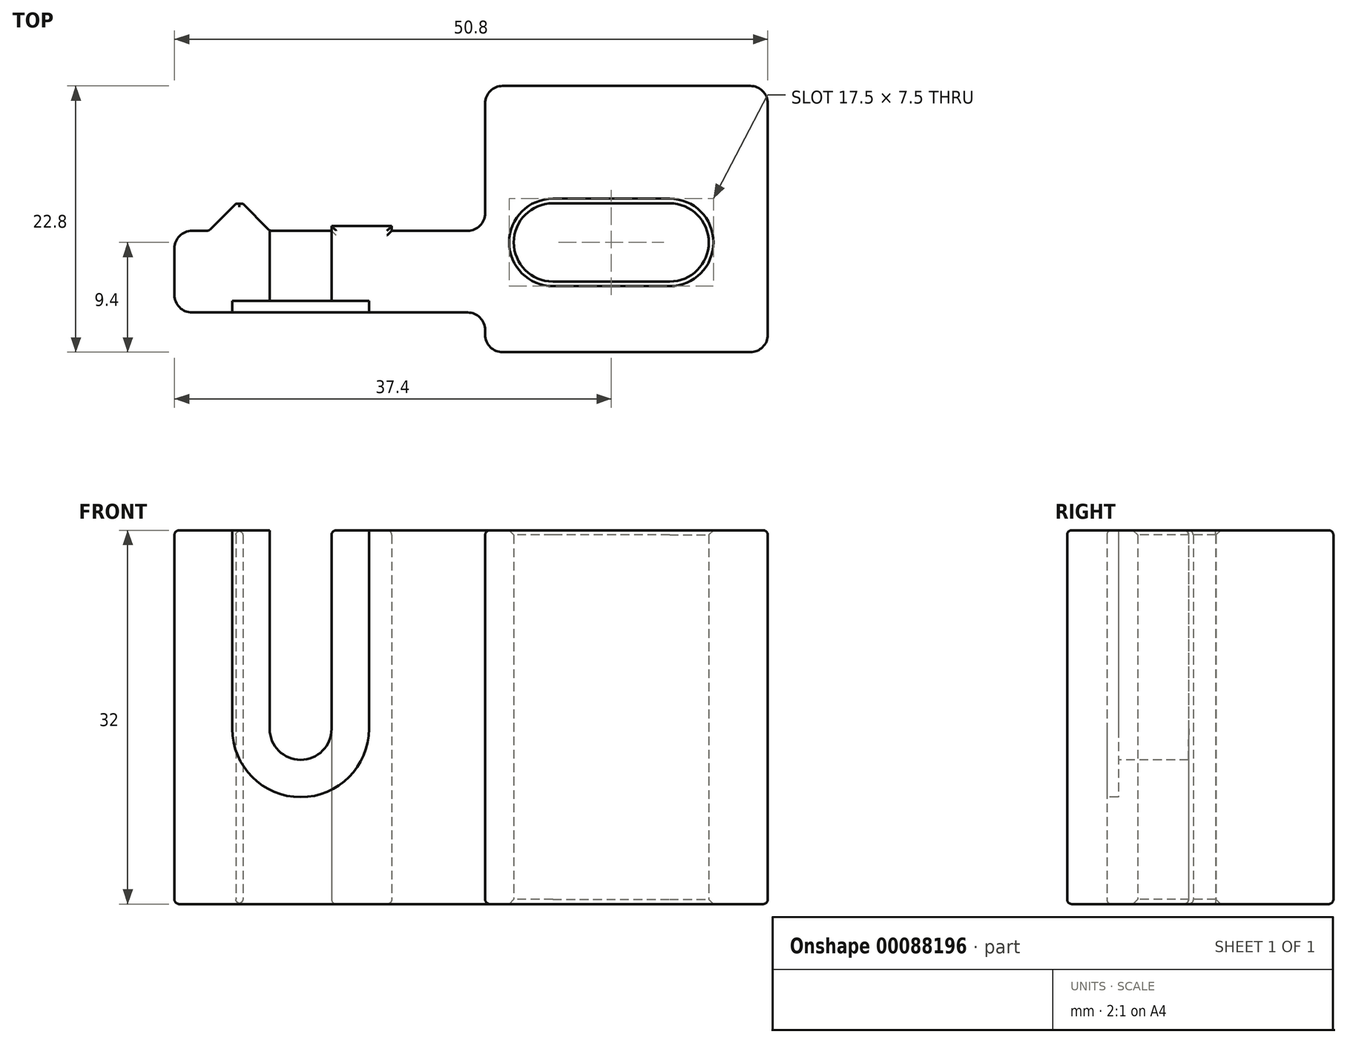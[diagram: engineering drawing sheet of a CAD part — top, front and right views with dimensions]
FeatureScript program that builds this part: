
annotation { "Feature Type Name" : "Feature", "Feature Type Description" : "" }
export const myFeature = defineFeature(function(context is Context, id is Id, definition is map)
    precondition{}
    {
        {
            var Q0;
            Q0=qCreatedBy(makeId("Top.planeOp"),FACE);
            var sketch = newSketch(context, id + "F0", { "sketchPlane" : qUnion([Q0])});
            skLineSegment(sketch, "E0", {"start": v(-10.8, 0) * mm, "end": v(-7.85, 0) * mm});
            skLineSegment(sketch, "E1", {"start": v(-2.65, 0) * mm, "end": v(2.65, 0) * mm});
            skLineSegment(sketch, "E2", {"start": v(2.65, 0) * mm, "end": v(2.65, 0.4) * mm});
            skLineSegment(sketch, "E3", {"start": v(2.65, 0.4) * mm, "end": v(7.8, 0.4) * mm});
            skLineSegment(sketch, "E4", {"start": v(7.8, 0.4) * mm, "end": v(7.8, 0) * mm});
            skLineSegment(sketch, "E5", {"start": v(7.8, 0) * mm, "end": v(15.8, 0) * mm});
            skLineSegment(sketch, "E6", {"start": v(15.8, 0) * mm, "end": v(15.8, 12.4) * mm});
            skLineSegment(sketch, "E7", {"start": v(15.8, 12.4) * mm, "end": v(40, 12.4) * mm});
            skLineSegment(sketch, "E8", {"start": v(40, 12.4) * mm, "end": v(40, -10.4) * mm});
            skLineSegment(sketch, "E9", {"start": v(40, -10.4) * mm, "end": v(15.8, -10.4) * mm});
            skLineSegment(sketch, "E10", {"start": v(15.8, -10.4) * mm, "end": v(15.8, -7) * mm});
            skLineSegment(sketch, "E11", {"start": v(15.8, -7) * mm, "end": v(-10.8, -7) * mm});
            skLineSegment(sketch, "E12", {"start": v(-10.8, -7) * mm, "end": v(-10.8, 0) * mm});
            skArc(sketch, "E13", {"start": v(21.6, 2.35) * mm, "mid": v(18.25, -1) * mm, "end": v(21.6, -4.35) * mm});
            skLineSegment(sketch, "E14", {"start": v(-7.85, 0) * mm, "end": v(-5.55, 2.3) * mm});
            skLineSegment(sketch, "E15", {"start": v(-4.95, 2.3) * mm, "end": v(-2.65, 0) * mm});
            skArc(sketch, "E16", {"start": v(31.6, -4.35) * mm, "mid": v(34.95, -1) * mm, "end": v(31.6, 2.35) * mm});
            skLineSegment(sketch, "E17", {"start": v(21.6, 2.35) * mm, "end": v(31.6, 2.35) * mm});
            skLineSegment(sketch, "E18", {"start": v(21.6, -4.35) * mm, "end": v(31.6, -4.35) * mm});
            skLineSegment(sketch, "E19", {"start": v(-5.55, 2.3) * mm, "end": v(-4.95, 2.3) * mm});
            skPoint(sketch, "E20.orphan", {"position": v(-5.25, 2.6) * mm});
            skSolve(sketch);
        }
        {
            var Q0;
            Q0=makeQuery(id+"F0.imprint","IMPRINT",FACE,{"disambiguationData":[TD([[makeQuery(id+"F0.imprint","IMPRINT",EDGE,{"derivedFrom":sQuery(id+"F0.wireOp",EDGE,"E0")}),-1.0]])]});
            extrude(context, id + "F1", {"entities" : qUnion([Q0]), "depth" : 32 * mm});
        }
        {
            var Q0;
            Q0=makeQuery(id+"F1.opExtrude","SWEPT_EDGE",EDGE,{"disambiguationData":[OSD([sQuery(id+"F0.wireOp",EDGE,"E0"),sQuery(id+"F0.wireOp",EDGE,"E14")])]});
            var Q1;
            Q1=makeQuery(id+"F1.opExtrude","SWEPT_EDGE",EDGE,{"disambiguationData":[OSD([sQuery(id+"F0.wireOp",EDGE,"E1"),sQuery(id+"F0.wireOp",EDGE,"E15")])]});
            fillet(context, id + "F2", {"entities" : qUnion([Q0, Q1]), "radius" : 0.4 * mm, "tangentPropagation" : true, "allowEdgeOverflow" : false});
        }
        {
            var Q0;
            Q0=makeQuery(id+"F1.opExtrude","SWEPT_EDGE",EDGE,{"disambiguationData":[OSD([sQuery(id+"F0.wireOp",EDGE,"E0"),sQuery(id+"F0.wireOp",EDGE,"E12")])]});
            var Q1;
            Q1=makeQuery(id+"F1.opExtrude","SWEPT_EDGE",EDGE,{"disambiguationData":[OSD([sQuery(id+"F0.wireOp",EDGE,"E11"),sQuery(id+"F0.wireOp",EDGE,"E12")])]});
            var Q2;
            Q2=makeQuery(id+"F1.opExtrude","SWEPT_EDGE",EDGE,{"disambiguationData":[OSD([sQuery(id+"F0.wireOp",EDGE,"E6"),sQuery(id+"F0.wireOp",EDGE,"E7")])]});
            var Q3;
            Q3=makeQuery(id+"F1.opExtrude","SWEPT_EDGE",EDGE,{"disambiguationData":[OSD([sQuery(id+"F0.wireOp",EDGE,"E7"),sQuery(id+"F0.wireOp",EDGE,"E8")])]});
            var Q4;
            Q4=makeQuery(id+"F1.opExtrude","SWEPT_EDGE",EDGE,{"disambiguationData":[OSD([sQuery(id+"F0.wireOp",EDGE,"E9"),sQuery(id+"F0.wireOp",EDGE,"E10")])]});
            var Q5;
            Q5=makeQuery(id+"F1.opExtrude","SWEPT_EDGE",EDGE,{"disambiguationData":[OSD([sQuery(id+"F0.wireOp",EDGE,"E8"),sQuery(id+"F0.wireOp",EDGE,"E9")])]});
            var Q6;
            Q6=makeQuery(id+"F1.opExtrude","SWEPT_EDGE",EDGE,{"disambiguationData":[OSD([sQuery(id+"F0.wireOp",EDGE,"E10"),sQuery(id+"F0.wireOp",EDGE,"E11")])]});
            var Q7;
            Q7=makeQuery(id+"F1.opExtrude","SWEPT_EDGE",EDGE,{"disambiguationData":[OSD([sQuery(id+"F0.wireOp",EDGE,"E5"),sQuery(id+"F0.wireOp",EDGE,"E6")])]});
            fillet(context, id + "F3", {"entities" : qUnion([Q0, Q1, Q2, Q3, Q4, Q5, Q6, Q7]), "radius" : 1.5 * mm, "tangentPropagation" : true, "allowEdgeOverflow" : false});
        }
        {
            var Q0;
            Q0=makeQuery(id+"F1.opExtrude","SWEPT_FACE",FACE,{"disambiguationData":[OSD([sQuery(id+"F0.wireOp",EDGE,"E11")])]});
            var sketch = newSketch(context, id + "F4", { "sketchPlane" : qUnion([Q0])});
            skLineSegment(sketch, "E21.left", {"start": v(2.65, 32) * mm, "end": v(2.65, 15) * mm});
            skLineSegment(sketch, "E21.right", {"start": v(-2.65, 32) * mm, "end": v(-2.65, 15) * mm});
            skArc(sketch, "E22", {"start": v(-2.65, 15) * mm, "mid": v(0, 12.35) * mm, "end": v(2.65, 15) * mm});
            skLineSegment(sketch, "E23", {"start": v(-5.85, 32) * mm, "end": v(-5.85, 15) * mm});
            skLineSegment(sketch, "E24", {"start": v(5.85, 32) * mm, "end": v(5.85, 15) * mm});
            skArc(sketch, "E25", {"start": v(-5.85, 15) * mm, "mid": v(0, 9.15) * mm, "end": v(5.85, 15) * mm});
            skSolve(sketch);
        }
        {
            var Q0;
            {var subQ0=sQuery(id+"F4.wireOp",EDGE,"E21.left");Q0=makeQuery(id+"F4.imprint","IMPRINT",FACE,{"disambiguationData":[TD([[makeQuery(id+"F4.imprint","IMPRINT",EDGE,{"derivedFrom":subQ0}),-1.0]])]});}
            extrude(context, id + "F5", {"entities" : qUnion([Q0]), "operationType" : NewBodyOperationType.REMOVE, "endBound" : BoundingType.THROUGH_ALL, "oppositeDirection" : true, "depth" : 25 * mm});
        }
        {
            var Q0;
            {var subQ1=sQuery(id+"F4.wireOp",EDGE,"E21.left");Q0=makeQuery(id+"F4.imprint","IMPRINT",FACE,{"disambiguationData":[TD([[makeQuery(id+"F4.imprint","IMPRINT",EDGE,{"derivedFrom":subQ1}),1.0]])]});}
            extrude(context, id + "F6", {"entities" : qUnion([Q0]), "operationType" : NewBodyOperationType.REMOVE, "oppositeDirection" : true, "depth" : 1 * mm});
        }
        {
            var Q0;
            {var subQ0=sQuery(id+"F0.wireOp",EDGE,"E12");var subQ1=sQuery(id+"F0.wireOp",EDGE,"E0");Q0=makeQuery(id+"F3.opFillet","BLEND_EDGE",EDGE,{"blendedFrom":[makeQuery(id+"F1.opExtrude","SWEPT_EDGE",EDGE,{"disambiguationData":[OSD([subQ1,subQ0])]}),makeQuery(id+"F1.opExtrude","CAP_FACE",FACE,{"disambiguationData":[OSD([subQ1,sQuery(id+"F0.wireOp",EDGE,"E1"),sQuery(id+"F0.wireOp",EDGE,"E2"),sQuery(id+"F0.wireOp",EDGE,"E3"),sQuery(id+"F0.wireOp",EDGE,"E4"),sQuery(id+"F0.wireOp",EDGE,"E5"),sQuery(id+"F0.wireOp",EDGE,"E6"),sQuery(id+"F0.wireOp",EDGE,"E7"),sQuery(id+"F0.wireOp",EDGE,"E8"),sQuery(id+"F0.wireOp",EDGE,"E9"),sQuery(id+"F0.wireOp",EDGE,"E10"),sQuery(id+"F0.wireOp",EDGE,"E11"),subQ0,sQuery(id+"F0.wireOp",EDGE,"E13"),sQuery(id+"F0.wireOp",EDGE,"E14"),sQuery(id+"F0.wireOp",EDGE,"E15")])],"isStart":false})],"blendedInto":[makeQuery(id+"F1.opExtrude","CAP_FACE",FACE,{"disambiguationData":[OSD([subQ1,sQuery(id+"F0.wireOp",EDGE,"E1"),sQuery(id+"F0.wireOp",EDGE,"E2"),sQuery(id+"F0.wireOp",EDGE,"E3"),sQuery(id+"F0.wireOp",EDGE,"E4"),sQuery(id+"F0.wireOp",EDGE,"E5"),sQuery(id+"F0.wireOp",EDGE,"E6"),sQuery(id+"F0.wireOp",EDGE,"E7"),sQuery(id+"F0.wireOp",EDGE,"E8"),sQuery(id+"F0.wireOp",EDGE,"E9"),sQuery(id+"F0.wireOp",EDGE,"E10"),sQuery(id+"F0.wireOp",EDGE,"E11"),subQ0,sQuery(id+"F0.wireOp",EDGE,"E13"),sQuery(id+"F0.wireOp",EDGE,"E14"),sQuery(id+"F0.wireOp",EDGE,"E15")])],"isStart":false})]});}
            var Q1;
            Q1=makeQuery(id+"F1.opExtrude","CAP_EDGE",EDGE,{"disambiguationData":[OSD([sQuery(id+"F0.wireOp",EDGE,"E0")])],"isStart":false});
            var Q2;
            Q2=makeQuery(id+"F1.opExtrude","CAP_EDGE",EDGE,{"disambiguationData":[OSD([sQuery(id+"F0.wireOp",EDGE,"E14")])],"isStart":false});
            var Q3;
            {var subQ0=sQuery(id+"F0.wireOp",EDGE,"E15");var subQ1=sQuery(id+"F0.wireOp",EDGE,"E14");Q3=makeQuery(id+"F2.opFillet","BLEND_EDGE",EDGE,{"blendedFrom":[makeQuery(id+"F1.opExtrude","SWEPT_EDGE",EDGE,{"disambiguationData":[OSD([subQ1,subQ0])]}),makeQuery(id+"F1.opExtrude","CAP_FACE",FACE,{"disambiguationData":[OSD([sQuery(id+"F0.wireOp",EDGE,"E0"),sQuery(id+"F0.wireOp",EDGE,"E1"),sQuery(id+"F0.wireOp",EDGE,"E2"),sQuery(id+"F0.wireOp",EDGE,"E3"),sQuery(id+"F0.wireOp",EDGE,"E4"),sQuery(id+"F0.wireOp",EDGE,"E5"),sQuery(id+"F0.wireOp",EDGE,"E6"),sQuery(id+"F0.wireOp",EDGE,"E7"),sQuery(id+"F0.wireOp",EDGE,"E8"),sQuery(id+"F0.wireOp",EDGE,"E9"),sQuery(id+"F0.wireOp",EDGE,"E10"),sQuery(id+"F0.wireOp",EDGE,"E11"),sQuery(id+"F0.wireOp",EDGE,"E12"),sQuery(id+"F0.wireOp",EDGE,"E13"),subQ1,subQ0])],"isStart":false})],"blendedInto":[makeQuery(id+"F1.opExtrude","CAP_FACE",FACE,{"disambiguationData":[OSD([sQuery(id+"F0.wireOp",EDGE,"E0"),sQuery(id+"F0.wireOp",EDGE,"E1"),sQuery(id+"F0.wireOp",EDGE,"E2"),sQuery(id+"F0.wireOp",EDGE,"E3"),sQuery(id+"F0.wireOp",EDGE,"E4"),sQuery(id+"F0.wireOp",EDGE,"E5"),sQuery(id+"F0.wireOp",EDGE,"E6"),sQuery(id+"F0.wireOp",EDGE,"E7"),sQuery(id+"F0.wireOp",EDGE,"E8"),sQuery(id+"F0.wireOp",EDGE,"E9"),sQuery(id+"F0.wireOp",EDGE,"E10"),sQuery(id+"F0.wireOp",EDGE,"E11"),sQuery(id+"F0.wireOp",EDGE,"E12"),sQuery(id+"F0.wireOp",EDGE,"E13"),subQ1,subQ0])],"isStart":false})]});}
            var Q4;
            Q4=makeQuery(id+"F1.opExtrude","CAP_EDGE",EDGE,{"disambiguationData":[OSD([sQuery(id+"F0.wireOp",EDGE,"E15")])],"isStart":false});
            var Q5;
            Q5=makeQuery(id+"F5.boolean.opBoolean","COPY",EDGE,{"derivedFrom":makeQuery(id+"F5.opExtrude","SWEPT_EDGE",EDGE,{"disambiguationData":[OSD([sQuery(id+"F0.wireOp",EDGE,"E11"),sQuery(id+"F4.wireOp",EDGE,"E21.right")])]})});
            var Q6;
            {var subQ0=sQuery(id+"F0.wireOp",EDGE,"E11");var subQ1=makeQuery(id+"F1.opExtrude","CAP_EDGE",EDGE,{"disambiguationData":[OSD([subQ0])],"isStart":false});Q6=makeQuery(id+"F6.boolean.opBoolean","COPY",EDGE,{"derivedFrom":makeQuery(id+"F6.opExtrude","CAP_EDGE",EDGE,{"disambiguationData":[OSD([subQ0]),TDD([makeQuery(id+"F4.imprint","IMPRINT",EDGE,{"disambiguationData":[TD([[makeQuery(id+"F4.imprint","INTERSECT",VERTEX,{"derivedFrom":[subQ1,sQuery(id+"F4.wireOp",EDGE,"E21.right")]}),-1.0]])],"derivedFrom":subQ1})])],"isStart":false})});}
            var Q7;
            Q7=makeQuery(id+"F6.boolean.opBoolean","COPY",EDGE,{"derivedFrom":makeQuery(id+"F6.opExtrude","SWEPT_EDGE",EDGE,{"disambiguationData":[OSD([sQuery(id+"F0.wireOp",EDGE,"E11"),sQuery(id+"F4.wireOp",EDGE,"E23")])]})});
            var Q8;
            {var subQ1=sQuery(id+"F0.wireOp",EDGE,"E11");Q8=makeQuery(id+"F5.boolean.opBoolean","SPLIT",EDGE,{"disambiguationData":[TD([makeQuery(id+"F5.opExtrude","SWEPT_FACE",FACE,{"disambiguationData":[OSD([sQuery(id+"F4.wireOp",EDGE,"E21.right")])]})])],"derivedFrom":makeQuery(id+"F1.opExtrude","CAP_EDGE",EDGE,{"disambiguationData":[OSD([subQ1])],"isStart":false})});}
            var Q9;
            {var subQ0=sQuery(id+"F0.wireOp",EDGE,"E12");var subQ1=sQuery(id+"F0.wireOp",EDGE,"E11");Q9=makeQuery(id+"F3.opFillet","BLEND_EDGE",EDGE,{"blendedFrom":[makeQuery(id+"F1.opExtrude","SWEPT_EDGE",EDGE,{"disambiguationData":[OSD([subQ1,subQ0])]}),makeQuery(id+"F1.opExtrude","CAP_FACE",FACE,{"disambiguationData":[OSD([sQuery(id+"F0.wireOp",EDGE,"E0"),sQuery(id+"F0.wireOp",EDGE,"E1"),sQuery(id+"F0.wireOp",EDGE,"E2"),sQuery(id+"F0.wireOp",EDGE,"E3"),sQuery(id+"F0.wireOp",EDGE,"E4"),sQuery(id+"F0.wireOp",EDGE,"E5"),sQuery(id+"F0.wireOp",EDGE,"E6"),sQuery(id+"F0.wireOp",EDGE,"E7"),sQuery(id+"F0.wireOp",EDGE,"E8"),sQuery(id+"F0.wireOp",EDGE,"E9"),sQuery(id+"F0.wireOp",EDGE,"E10"),subQ1,subQ0,sQuery(id+"F0.wireOp",EDGE,"E13"),sQuery(id+"F0.wireOp",EDGE,"E14"),sQuery(id+"F0.wireOp",EDGE,"E15")])],"isStart":false})],"blendedInto":[makeQuery(id+"F1.opExtrude","CAP_FACE",FACE,{"disambiguationData":[OSD([sQuery(id+"F0.wireOp",EDGE,"E0"),sQuery(id+"F0.wireOp",EDGE,"E1"),sQuery(id+"F0.wireOp",EDGE,"E2"),sQuery(id+"F0.wireOp",EDGE,"E3"),sQuery(id+"F0.wireOp",EDGE,"E4"),sQuery(id+"F0.wireOp",EDGE,"E5"),sQuery(id+"F0.wireOp",EDGE,"E6"),sQuery(id+"F0.wireOp",EDGE,"E7"),sQuery(id+"F0.wireOp",EDGE,"E8"),sQuery(id+"F0.wireOp",EDGE,"E9"),sQuery(id+"F0.wireOp",EDGE,"E10"),subQ1,subQ0,sQuery(id+"F0.wireOp",EDGE,"E13"),sQuery(id+"F0.wireOp",EDGE,"E14"),sQuery(id+"F0.wireOp",EDGE,"E15")])],"isStart":false})]});}
            var Q10;
            Q10=makeQuery(id+"F1.opExtrude","CAP_EDGE",EDGE,{"disambiguationData":[OSD([sQuery(id+"F0.wireOp",EDGE,"E12")])],"isStart":false});
            fillet(context, id + "F7", {"entities" : qUnion([Q0, Q1, Q2, Q3, Q4, Q5, Q6, Q7, Q8, Q9, Q10]), "radius" : 0.4 * mm, "tangentPropagation" : true, "allowEdgeOverflow" : false});
        }
        {
            var Q0;
            Q0=makeQuery(id+"F1.opExtrude","CAP_EDGE",EDGE,{"disambiguationData":[OSD([sQuery(id+"F0.wireOp",EDGE,"E7")])],"isStart":false});
            var Q1;
            {var subQ0=sQuery(id+"F0.wireOp",EDGE,"E7");var subQ1=sQuery(id+"F0.wireOp",EDGE,"E6");Q1=makeQuery(id+"F3.opFillet","BLEND_EDGE",EDGE,{"blendedFrom":[makeQuery(id+"F1.opExtrude","SWEPT_EDGE",EDGE,{"disambiguationData":[OSD([subQ1,subQ0])]}),makeQuery(id+"F1.opExtrude","CAP_FACE",FACE,{"disambiguationData":[OSD([sQuery(id+"F0.wireOp",EDGE,"E0"),sQuery(id+"F0.wireOp",EDGE,"E1"),sQuery(id+"F0.wireOp",EDGE,"E2"),sQuery(id+"F0.wireOp",EDGE,"E3"),sQuery(id+"F0.wireOp",EDGE,"E4"),sQuery(id+"F0.wireOp",EDGE,"E5"),subQ1,subQ0,sQuery(id+"F0.wireOp",EDGE,"E8"),sQuery(id+"F0.wireOp",EDGE,"E9"),sQuery(id+"F0.wireOp",EDGE,"E10"),sQuery(id+"F0.wireOp",EDGE,"E11"),sQuery(id+"F0.wireOp",EDGE,"E12"),sQuery(id+"F0.wireOp",EDGE,"E13"),sQuery(id+"F0.wireOp",EDGE,"E14"),sQuery(id+"F0.wireOp",EDGE,"E15")])],"isStart":false})],"blendedInto":[makeQuery(id+"F1.opExtrude","CAP_FACE",FACE,{"disambiguationData":[OSD([sQuery(id+"F0.wireOp",EDGE,"E0"),sQuery(id+"F0.wireOp",EDGE,"E1"),sQuery(id+"F0.wireOp",EDGE,"E2"),sQuery(id+"F0.wireOp",EDGE,"E3"),sQuery(id+"F0.wireOp",EDGE,"E4"),sQuery(id+"F0.wireOp",EDGE,"E5"),subQ1,subQ0,sQuery(id+"F0.wireOp",EDGE,"E8"),sQuery(id+"F0.wireOp",EDGE,"E9"),sQuery(id+"F0.wireOp",EDGE,"E10"),sQuery(id+"F0.wireOp",EDGE,"E11"),sQuery(id+"F0.wireOp",EDGE,"E12"),sQuery(id+"F0.wireOp",EDGE,"E13"),sQuery(id+"F0.wireOp",EDGE,"E14"),sQuery(id+"F0.wireOp",EDGE,"E15")])],"isStart":false})]});}
            var Q2;
            {var subQ0=sQuery(id+"F0.wireOp",EDGE,"E8");var subQ1=sQuery(id+"F0.wireOp",EDGE,"E7");Q2=makeQuery(id+"F3.opFillet","BLEND_EDGE",EDGE,{"blendedFrom":[makeQuery(id+"F1.opExtrude","SWEPT_EDGE",EDGE,{"disambiguationData":[OSD([subQ1,subQ0])]}),makeQuery(id+"F1.opExtrude","CAP_FACE",FACE,{"disambiguationData":[OSD([sQuery(id+"F0.wireOp",EDGE,"E0"),sQuery(id+"F0.wireOp",EDGE,"E1"),sQuery(id+"F0.wireOp",EDGE,"E2"),sQuery(id+"F0.wireOp",EDGE,"E3"),sQuery(id+"F0.wireOp",EDGE,"E4"),sQuery(id+"F0.wireOp",EDGE,"E5"),sQuery(id+"F0.wireOp",EDGE,"E6"),subQ1,subQ0,sQuery(id+"F0.wireOp",EDGE,"E9"),sQuery(id+"F0.wireOp",EDGE,"E10"),sQuery(id+"F0.wireOp",EDGE,"E11"),sQuery(id+"F0.wireOp",EDGE,"E12"),sQuery(id+"F0.wireOp",EDGE,"E13"),sQuery(id+"F0.wireOp",EDGE,"E14"),sQuery(id+"F0.wireOp",EDGE,"E15")])],"isStart":false})],"blendedInto":[makeQuery(id+"F1.opExtrude","CAP_FACE",FACE,{"disambiguationData":[OSD([sQuery(id+"F0.wireOp",EDGE,"E0"),sQuery(id+"F0.wireOp",EDGE,"E1"),sQuery(id+"F0.wireOp",EDGE,"E2"),sQuery(id+"F0.wireOp",EDGE,"E3"),sQuery(id+"F0.wireOp",EDGE,"E4"),sQuery(id+"F0.wireOp",EDGE,"E5"),sQuery(id+"F0.wireOp",EDGE,"E6"),subQ1,subQ0,sQuery(id+"F0.wireOp",EDGE,"E9"),sQuery(id+"F0.wireOp",EDGE,"E10"),sQuery(id+"F0.wireOp",EDGE,"E11"),sQuery(id+"F0.wireOp",EDGE,"E12"),sQuery(id+"F0.wireOp",EDGE,"E13"),sQuery(id+"F0.wireOp",EDGE,"E14"),sQuery(id+"F0.wireOp",EDGE,"E15")])],"isStart":false})]});}
            var Q3;
            Q3=makeQuery(id+"F1.opExtrude","CAP_EDGE",EDGE,{"disambiguationData":[OSD([sQuery(id+"F0.wireOp",EDGE,"E8")])],"isStart":false});
            var Q4;
            {var subQ0=sQuery(id+"F0.wireOp",EDGE,"E9");var subQ1=sQuery(id+"F0.wireOp",EDGE,"E8");Q4=makeQuery(id+"F3.opFillet","BLEND_EDGE",EDGE,{"blendedFrom":[makeQuery(id+"F1.opExtrude","SWEPT_EDGE",EDGE,{"disambiguationData":[OSD([subQ1,subQ0])]}),makeQuery(id+"F1.opExtrude","CAP_FACE",FACE,{"disambiguationData":[OSD([sQuery(id+"F0.wireOp",EDGE,"E0"),sQuery(id+"F0.wireOp",EDGE,"E1"),sQuery(id+"F0.wireOp",EDGE,"E2"),sQuery(id+"F0.wireOp",EDGE,"E3"),sQuery(id+"F0.wireOp",EDGE,"E4"),sQuery(id+"F0.wireOp",EDGE,"E5"),sQuery(id+"F0.wireOp",EDGE,"E6"),sQuery(id+"F0.wireOp",EDGE,"E7"),subQ1,subQ0,sQuery(id+"F0.wireOp",EDGE,"E10"),sQuery(id+"F0.wireOp",EDGE,"E11"),sQuery(id+"F0.wireOp",EDGE,"E12"),sQuery(id+"F0.wireOp",EDGE,"E13"),sQuery(id+"F0.wireOp",EDGE,"E14"),sQuery(id+"F0.wireOp",EDGE,"E15")])],"isStart":false})],"blendedInto":[makeQuery(id+"F1.opExtrude","CAP_FACE",FACE,{"disambiguationData":[OSD([sQuery(id+"F0.wireOp",EDGE,"E0"),sQuery(id+"F0.wireOp",EDGE,"E1"),sQuery(id+"F0.wireOp",EDGE,"E2"),sQuery(id+"F0.wireOp",EDGE,"E3"),sQuery(id+"F0.wireOp",EDGE,"E4"),sQuery(id+"F0.wireOp",EDGE,"E5"),sQuery(id+"F0.wireOp",EDGE,"E6"),sQuery(id+"F0.wireOp",EDGE,"E7"),subQ1,subQ0,sQuery(id+"F0.wireOp",EDGE,"E10"),sQuery(id+"F0.wireOp",EDGE,"E11"),sQuery(id+"F0.wireOp",EDGE,"E12"),sQuery(id+"F0.wireOp",EDGE,"E13"),sQuery(id+"F0.wireOp",EDGE,"E14"),sQuery(id+"F0.wireOp",EDGE,"E15")])],"isStart":false})]});}
            var Q5;
            Q5=makeQuery(id+"F1.opExtrude","CAP_EDGE",EDGE,{"disambiguationData":[OSD([sQuery(id+"F0.wireOp",EDGE,"E9")])],"isStart":false});
            var Q6;
            {var subQ0=sQuery(id+"F0.wireOp",EDGE,"E10");var subQ1=sQuery(id+"F0.wireOp",EDGE,"E9");Q6=makeQuery(id+"F3.opFillet","BLEND_EDGE",EDGE,{"blendedFrom":[makeQuery(id+"F1.opExtrude","SWEPT_EDGE",EDGE,{"disambiguationData":[OSD([subQ1,subQ0])]}),makeQuery(id+"F1.opExtrude","CAP_FACE",FACE,{"disambiguationData":[OSD([sQuery(id+"F0.wireOp",EDGE,"E0"),sQuery(id+"F0.wireOp",EDGE,"E1"),sQuery(id+"F0.wireOp",EDGE,"E2"),sQuery(id+"F0.wireOp",EDGE,"E3"),sQuery(id+"F0.wireOp",EDGE,"E4"),sQuery(id+"F0.wireOp",EDGE,"E5"),sQuery(id+"F0.wireOp",EDGE,"E6"),sQuery(id+"F0.wireOp",EDGE,"E7"),sQuery(id+"F0.wireOp",EDGE,"E8"),subQ1,subQ0,sQuery(id+"F0.wireOp",EDGE,"E11"),sQuery(id+"F0.wireOp",EDGE,"E12"),sQuery(id+"F0.wireOp",EDGE,"E13"),sQuery(id+"F0.wireOp",EDGE,"E14"),sQuery(id+"F0.wireOp",EDGE,"E15")])],"isStart":false})],"blendedInto":[makeQuery(id+"F1.opExtrude","CAP_FACE",FACE,{"disambiguationData":[OSD([sQuery(id+"F0.wireOp",EDGE,"E0"),sQuery(id+"F0.wireOp",EDGE,"E1"),sQuery(id+"F0.wireOp",EDGE,"E2"),sQuery(id+"F0.wireOp",EDGE,"E3"),sQuery(id+"F0.wireOp",EDGE,"E4"),sQuery(id+"F0.wireOp",EDGE,"E5"),sQuery(id+"F0.wireOp",EDGE,"E6"),sQuery(id+"F0.wireOp",EDGE,"E7"),sQuery(id+"F0.wireOp",EDGE,"E8"),subQ1,subQ0,sQuery(id+"F0.wireOp",EDGE,"E11"),sQuery(id+"F0.wireOp",EDGE,"E12"),sQuery(id+"F0.wireOp",EDGE,"E13"),sQuery(id+"F0.wireOp",EDGE,"E14"),sQuery(id+"F0.wireOp",EDGE,"E15")])],"isStart":false})]});}
            var Q7;
            Q7=makeQuery(id+"F1.opExtrude","CAP_EDGE",EDGE,{"disambiguationData":[OSD([sQuery(id+"F0.wireOp",EDGE,"E10")])],"isStart":false});
            var Q8;
            {var subQ0=sQuery(id+"F0.wireOp",EDGE,"E11");var subQ2=sQuery(id+"F0.wireOp",EDGE,"E2");Q8=makeQuery(id+"F5.boolean.opBoolean","SPLIT",EDGE,{"disambiguationData":[TD([makeQuery(id+"F1.opExtrude","SWEPT_FACE",FACE,{"disambiguationData":[OSD([subQ2])]})])],"derivedFrom":makeQuery(id+"F1.opExtrude","CAP_EDGE",EDGE,{"disambiguationData":[OSD([subQ0])],"isStart":false})});}
            var Q9;
            Q9=makeQuery(id+"F6.boolean.opBoolean","COPY",EDGE,{"derivedFrom":makeQuery(id+"F6.opExtrude","SWEPT_EDGE",EDGE,{"disambiguationData":[OSD([sQuery(id+"F0.wireOp",EDGE,"E11"),sQuery(id+"F4.wireOp",EDGE,"E24")])]})});
            var Q10;
            {var subQ0=sQuery(id+"F0.wireOp",EDGE,"E11");var subQ1=makeQuery(id+"F1.opExtrude","CAP_EDGE",EDGE,{"disambiguationData":[OSD([subQ0])],"isStart":false});Q10=makeQuery(id+"F6.boolean.opBoolean","COPY",EDGE,{"derivedFrom":makeQuery(id+"F6.opExtrude","CAP_EDGE",EDGE,{"disambiguationData":[OSD([subQ0]),TDD([makeQuery(id+"F4.imprint","IMPRINT",EDGE,{"disambiguationData":[TD([[makeQuery(id+"F4.imprint","INTERSECT",VERTEX,{"derivedFrom":[subQ1,sQuery(id+"F4.wireOp",EDGE,"E21.left")]}),1.0]])],"derivedFrom":subQ1})])],"isStart":false})});}
            var Q11;
            Q11=makeQuery(id+"F5.boolean.opBoolean","MERGE",EDGE,{"derivedFrom":[makeQuery(id+"F1.opExtrude","CAP_EDGE",EDGE,{"disambiguationData":[OSD([sQuery(id+"F0.wireOp",EDGE,"E2")])],"isStart":false}),makeQuery(id+"F5.opExtrude","SWEPT_EDGE",EDGE,{"disambiguationData":[OSD([sQuery(id+"F0.wireOp",EDGE,"E11"),sQuery(id+"F4.wireOp",EDGE,"E21.left")])]})]});
            var Q12;
            Q12=makeQuery(id+"F1.opExtrude","CAP_EDGE",EDGE,{"disambiguationData":[OSD([sQuery(id+"F0.wireOp",EDGE,"E3")])],"isStart":false});
            var Q13;
            Q13=makeQuery(id+"F1.opExtrude","CAP_EDGE",EDGE,{"disambiguationData":[OSD([sQuery(id+"F0.wireOp",EDGE,"E4")])],"isStart":false});
            var Q14;
            Q14=makeQuery(id+"F1.opExtrude","CAP_EDGE",EDGE,{"disambiguationData":[OSD([sQuery(id+"F0.wireOp",EDGE,"E5")])],"isStart":false});
            var Q15;
            Q15=makeQuery(id+"F1.opExtrude","CAP_EDGE",EDGE,{"disambiguationData":[OSD([sQuery(id+"F0.wireOp",EDGE,"E6")])],"isStart":false});
            fillet(context, id + "F8", {"entities" : qUnion([Q0, Q1, Q2, Q3, Q4, Q5, Q6, Q7, Q8, Q9, Q10, Q11, Q12, Q13, Q14, Q15]), "radius" : 0.4 * mm, "tangentPropagation" : true, "allowEdgeOverflow" : false});
        }
        {
            var Q0;
            Q0=makeQuery(id+"F1.opExtrude","CAP_EDGE",EDGE,{"disambiguationData":[OSD([sQuery(id+"F0.wireOp",EDGE,"E11")])],"isStart":true});
            var Q1;
            {var subQ0=sQuery(id+"F0.wireOp",EDGE,"E12");var subQ1=sQuery(id+"F0.wireOp",EDGE,"E11");Q1=makeQuery(id+"F3.opFillet","BLEND_EDGE",EDGE,{"blendedFrom":[makeQuery(id+"F1.opExtrude","SWEPT_EDGE",EDGE,{"disambiguationData":[OSD([subQ1,subQ0])]}),makeQuery(id+"F1.opExtrude","CAP_FACE",FACE,{"disambiguationData":[OSD([sQuery(id+"F0.wireOp",EDGE,"E0"),sQuery(id+"F0.wireOp",EDGE,"E1"),sQuery(id+"F0.wireOp",EDGE,"E2"),sQuery(id+"F0.wireOp",EDGE,"E3"),sQuery(id+"F0.wireOp",EDGE,"E4"),sQuery(id+"F0.wireOp",EDGE,"E5"),sQuery(id+"F0.wireOp",EDGE,"E6"),sQuery(id+"F0.wireOp",EDGE,"E7"),sQuery(id+"F0.wireOp",EDGE,"E8"),sQuery(id+"F0.wireOp",EDGE,"E9"),sQuery(id+"F0.wireOp",EDGE,"E10"),subQ1,subQ0,sQuery(id+"F0.wireOp",EDGE,"E13"),sQuery(id+"F0.wireOp",EDGE,"E14"),sQuery(id+"F0.wireOp",EDGE,"E15")])],"isStart":true})],"blendedInto":[makeQuery(id+"F1.opExtrude","CAP_FACE",FACE,{"disambiguationData":[OSD([sQuery(id+"F0.wireOp",EDGE,"E0"),sQuery(id+"F0.wireOp",EDGE,"E1"),sQuery(id+"F0.wireOp",EDGE,"E2"),sQuery(id+"F0.wireOp",EDGE,"E3"),sQuery(id+"F0.wireOp",EDGE,"E4"),sQuery(id+"F0.wireOp",EDGE,"E5"),sQuery(id+"F0.wireOp",EDGE,"E6"),sQuery(id+"F0.wireOp",EDGE,"E7"),sQuery(id+"F0.wireOp",EDGE,"E8"),sQuery(id+"F0.wireOp",EDGE,"E9"),sQuery(id+"F0.wireOp",EDGE,"E10"),subQ1,subQ0,sQuery(id+"F0.wireOp",EDGE,"E13"),sQuery(id+"F0.wireOp",EDGE,"E14"),sQuery(id+"F0.wireOp",EDGE,"E15")])],"isStart":true})]});}
            var Q2;
            Q2=makeQuery(id+"F1.opExtrude","CAP_EDGE",EDGE,{"disambiguationData":[OSD([sQuery(id+"F0.wireOp",EDGE,"E12")])],"isStart":true});
            var Q3;
            {var subQ0=sQuery(id+"F0.wireOp",EDGE,"E12");var subQ1=sQuery(id+"F0.wireOp",EDGE,"E0");Q3=makeQuery(id+"F3.opFillet","BLEND_EDGE",EDGE,{"blendedFrom":[makeQuery(id+"F1.opExtrude","SWEPT_EDGE",EDGE,{"disambiguationData":[OSD([subQ1,subQ0])]}),makeQuery(id+"F1.opExtrude","CAP_FACE",FACE,{"disambiguationData":[OSD([subQ1,sQuery(id+"F0.wireOp",EDGE,"E1"),sQuery(id+"F0.wireOp",EDGE,"E2"),sQuery(id+"F0.wireOp",EDGE,"E3"),sQuery(id+"F0.wireOp",EDGE,"E4"),sQuery(id+"F0.wireOp",EDGE,"E5"),sQuery(id+"F0.wireOp",EDGE,"E6"),sQuery(id+"F0.wireOp",EDGE,"E7"),sQuery(id+"F0.wireOp",EDGE,"E8"),sQuery(id+"F0.wireOp",EDGE,"E9"),sQuery(id+"F0.wireOp",EDGE,"E10"),sQuery(id+"F0.wireOp",EDGE,"E11"),subQ0,sQuery(id+"F0.wireOp",EDGE,"E13"),sQuery(id+"F0.wireOp",EDGE,"E14"),sQuery(id+"F0.wireOp",EDGE,"E15")])],"isStart":true})],"blendedInto":[makeQuery(id+"F1.opExtrude","CAP_FACE",FACE,{"disambiguationData":[OSD([subQ1,sQuery(id+"F0.wireOp",EDGE,"E1"),sQuery(id+"F0.wireOp",EDGE,"E2"),sQuery(id+"F0.wireOp",EDGE,"E3"),sQuery(id+"F0.wireOp",EDGE,"E4"),sQuery(id+"F0.wireOp",EDGE,"E5"),sQuery(id+"F0.wireOp",EDGE,"E6"),sQuery(id+"F0.wireOp",EDGE,"E7"),sQuery(id+"F0.wireOp",EDGE,"E8"),sQuery(id+"F0.wireOp",EDGE,"E9"),sQuery(id+"F0.wireOp",EDGE,"E10"),sQuery(id+"F0.wireOp",EDGE,"E11"),subQ0,sQuery(id+"F0.wireOp",EDGE,"E13"),sQuery(id+"F0.wireOp",EDGE,"E14"),sQuery(id+"F0.wireOp",EDGE,"E15")])],"isStart":true})]});}
            var Q4;
            Q4=makeQuery(id+"F1.opExtrude","CAP_EDGE",EDGE,{"disambiguationData":[OSD([sQuery(id+"F0.wireOp",EDGE,"E0")])],"isStart":true});
            var Q5;
            Q5=makeQuery(id+"F1.opExtrude","CAP_EDGE",EDGE,{"disambiguationData":[OSD([sQuery(id+"F0.wireOp",EDGE,"E14")])],"isStart":true});
            var Q6;
            {var subQ0=sQuery(id+"F0.wireOp",EDGE,"E15");var subQ1=sQuery(id+"F0.wireOp",EDGE,"E14");Q6=makeQuery(id+"F2.opFillet","BLEND_EDGE",EDGE,{"blendedFrom":[makeQuery(id+"F1.opExtrude","SWEPT_EDGE",EDGE,{"disambiguationData":[OSD([subQ1,subQ0])]}),makeQuery(id+"F1.opExtrude","CAP_FACE",FACE,{"disambiguationData":[OSD([sQuery(id+"F0.wireOp",EDGE,"E0"),sQuery(id+"F0.wireOp",EDGE,"E1"),sQuery(id+"F0.wireOp",EDGE,"E2"),sQuery(id+"F0.wireOp",EDGE,"E3"),sQuery(id+"F0.wireOp",EDGE,"E4"),sQuery(id+"F0.wireOp",EDGE,"E5"),sQuery(id+"F0.wireOp",EDGE,"E6"),sQuery(id+"F0.wireOp",EDGE,"E7"),sQuery(id+"F0.wireOp",EDGE,"E8"),sQuery(id+"F0.wireOp",EDGE,"E9"),sQuery(id+"F0.wireOp",EDGE,"E10"),sQuery(id+"F0.wireOp",EDGE,"E11"),sQuery(id+"F0.wireOp",EDGE,"E12"),sQuery(id+"F0.wireOp",EDGE,"E13"),subQ1,subQ0])],"isStart":true})],"blendedInto":[makeQuery(id+"F1.opExtrude","CAP_FACE",FACE,{"disambiguationData":[OSD([sQuery(id+"F0.wireOp",EDGE,"E0"),sQuery(id+"F0.wireOp",EDGE,"E1"),sQuery(id+"F0.wireOp",EDGE,"E2"),sQuery(id+"F0.wireOp",EDGE,"E3"),sQuery(id+"F0.wireOp",EDGE,"E4"),sQuery(id+"F0.wireOp",EDGE,"E5"),sQuery(id+"F0.wireOp",EDGE,"E6"),sQuery(id+"F0.wireOp",EDGE,"E7"),sQuery(id+"F0.wireOp",EDGE,"E8"),sQuery(id+"F0.wireOp",EDGE,"E9"),sQuery(id+"F0.wireOp",EDGE,"E10"),sQuery(id+"F0.wireOp",EDGE,"E11"),sQuery(id+"F0.wireOp",EDGE,"E12"),sQuery(id+"F0.wireOp",EDGE,"E13"),subQ1,subQ0])],"isStart":true})]});}
            var Q7;
            Q7=makeQuery(id+"F1.opExtrude","CAP_EDGE",EDGE,{"disambiguationData":[OSD([sQuery(id+"F0.wireOp",EDGE,"E15")])],"isStart":true});
            var Q8;
            Q8=makeQuery(id+"F1.opExtrude","CAP_EDGE",EDGE,{"disambiguationData":[OSD([sQuery(id+"F0.wireOp",EDGE,"E1")])],"isStart":true});
            var Q9;
            Q9=makeQuery(id+"F1.opExtrude","CAP_EDGE",EDGE,{"disambiguationData":[OSD([sQuery(id+"F0.wireOp",EDGE,"E2")])],"isStart":true});
            var Q10;
            Q10=makeQuery(id+"F1.opExtrude","CAP_EDGE",EDGE,{"disambiguationData":[OSD([sQuery(id+"F0.wireOp",EDGE,"E3")])],"isStart":true});
            var Q11;
            Q11=makeQuery(id+"F1.opExtrude","CAP_EDGE",EDGE,{"disambiguationData":[OSD([sQuery(id+"F0.wireOp",EDGE,"E4")])],"isStart":true});
            var Q12;
            Q12=makeQuery(id+"F1.opExtrude","CAP_EDGE",EDGE,{"disambiguationData":[OSD([sQuery(id+"F0.wireOp",EDGE,"E5")])],"isStart":true});
            var Q13;
            Q13=makeQuery(id+"F1.opExtrude","CAP_EDGE",EDGE,{"disambiguationData":[OSD([sQuery(id+"F0.wireOp",EDGE,"E6")])],"isStart":true});
            var Q14;
            {var subQ0=sQuery(id+"F0.wireOp",EDGE,"E7");var subQ1=sQuery(id+"F0.wireOp",EDGE,"E6");Q14=makeQuery(id+"F3.opFillet","BLEND_EDGE",EDGE,{"blendedFrom":[makeQuery(id+"F1.opExtrude","SWEPT_EDGE",EDGE,{"disambiguationData":[OSD([subQ1,subQ0])]}),makeQuery(id+"F1.opExtrude","CAP_FACE",FACE,{"disambiguationData":[OSD([sQuery(id+"F0.wireOp",EDGE,"E0"),sQuery(id+"F0.wireOp",EDGE,"E1"),sQuery(id+"F0.wireOp",EDGE,"E2"),sQuery(id+"F0.wireOp",EDGE,"E3"),sQuery(id+"F0.wireOp",EDGE,"E4"),sQuery(id+"F0.wireOp",EDGE,"E5"),subQ1,subQ0,sQuery(id+"F0.wireOp",EDGE,"E8"),sQuery(id+"F0.wireOp",EDGE,"E9"),sQuery(id+"F0.wireOp",EDGE,"E10"),sQuery(id+"F0.wireOp",EDGE,"E11"),sQuery(id+"F0.wireOp",EDGE,"E12"),sQuery(id+"F0.wireOp",EDGE,"E13"),sQuery(id+"F0.wireOp",EDGE,"E14"),sQuery(id+"F0.wireOp",EDGE,"E15")])],"isStart":true})],"blendedInto":[makeQuery(id+"F1.opExtrude","CAP_FACE",FACE,{"disambiguationData":[OSD([sQuery(id+"F0.wireOp",EDGE,"E0"),sQuery(id+"F0.wireOp",EDGE,"E1"),sQuery(id+"F0.wireOp",EDGE,"E2"),sQuery(id+"F0.wireOp",EDGE,"E3"),sQuery(id+"F0.wireOp",EDGE,"E4"),sQuery(id+"F0.wireOp",EDGE,"E5"),subQ1,subQ0,sQuery(id+"F0.wireOp",EDGE,"E8"),sQuery(id+"F0.wireOp",EDGE,"E9"),sQuery(id+"F0.wireOp",EDGE,"E10"),sQuery(id+"F0.wireOp",EDGE,"E11"),sQuery(id+"F0.wireOp",EDGE,"E12"),sQuery(id+"F0.wireOp",EDGE,"E13"),sQuery(id+"F0.wireOp",EDGE,"E14"),sQuery(id+"F0.wireOp",EDGE,"E15")])],"isStart":true})]});}
            var Q15;
            Q15=makeQuery(id+"F1.opExtrude","CAP_EDGE",EDGE,{"disambiguationData":[OSD([sQuery(id+"F0.wireOp",EDGE,"E7")])],"isStart":true});
            var Q16;
            {var subQ0=sQuery(id+"F0.wireOp",EDGE,"E8");var subQ1=sQuery(id+"F0.wireOp",EDGE,"E7");Q16=makeQuery(id+"F3.opFillet","BLEND_EDGE",EDGE,{"blendedFrom":[makeQuery(id+"F1.opExtrude","SWEPT_EDGE",EDGE,{"disambiguationData":[OSD([subQ1,subQ0])]}),makeQuery(id+"F1.opExtrude","CAP_FACE",FACE,{"disambiguationData":[OSD([sQuery(id+"F0.wireOp",EDGE,"E0"),sQuery(id+"F0.wireOp",EDGE,"E1"),sQuery(id+"F0.wireOp",EDGE,"E2"),sQuery(id+"F0.wireOp",EDGE,"E3"),sQuery(id+"F0.wireOp",EDGE,"E4"),sQuery(id+"F0.wireOp",EDGE,"E5"),sQuery(id+"F0.wireOp",EDGE,"E6"),subQ1,subQ0,sQuery(id+"F0.wireOp",EDGE,"E9"),sQuery(id+"F0.wireOp",EDGE,"E10"),sQuery(id+"F0.wireOp",EDGE,"E11"),sQuery(id+"F0.wireOp",EDGE,"E12"),sQuery(id+"F0.wireOp",EDGE,"E13"),sQuery(id+"F0.wireOp",EDGE,"E14"),sQuery(id+"F0.wireOp",EDGE,"E15")])],"isStart":true})],"blendedInto":[makeQuery(id+"F1.opExtrude","CAP_FACE",FACE,{"disambiguationData":[OSD([sQuery(id+"F0.wireOp",EDGE,"E0"),sQuery(id+"F0.wireOp",EDGE,"E1"),sQuery(id+"F0.wireOp",EDGE,"E2"),sQuery(id+"F0.wireOp",EDGE,"E3"),sQuery(id+"F0.wireOp",EDGE,"E4"),sQuery(id+"F0.wireOp",EDGE,"E5"),sQuery(id+"F0.wireOp",EDGE,"E6"),subQ1,subQ0,sQuery(id+"F0.wireOp",EDGE,"E9"),sQuery(id+"F0.wireOp",EDGE,"E10"),sQuery(id+"F0.wireOp",EDGE,"E11"),sQuery(id+"F0.wireOp",EDGE,"E12"),sQuery(id+"F0.wireOp",EDGE,"E13"),sQuery(id+"F0.wireOp",EDGE,"E14"),sQuery(id+"F0.wireOp",EDGE,"E15")])],"isStart":true})]});}
            var Q17;
            Q17=makeQuery(id+"F1.opExtrude","CAP_EDGE",EDGE,{"disambiguationData":[OSD([sQuery(id+"F0.wireOp",EDGE,"E8")])],"isStart":true});
            var Q18;
            {var subQ0=sQuery(id+"F0.wireOp",EDGE,"E9");var subQ1=sQuery(id+"F0.wireOp",EDGE,"E8");Q18=makeQuery(id+"F3.opFillet","BLEND_EDGE",EDGE,{"blendedFrom":[makeQuery(id+"F1.opExtrude","SWEPT_EDGE",EDGE,{"disambiguationData":[OSD([subQ1,subQ0])]}),makeQuery(id+"F1.opExtrude","CAP_FACE",FACE,{"disambiguationData":[OSD([sQuery(id+"F0.wireOp",EDGE,"E0"),sQuery(id+"F0.wireOp",EDGE,"E1"),sQuery(id+"F0.wireOp",EDGE,"E2"),sQuery(id+"F0.wireOp",EDGE,"E3"),sQuery(id+"F0.wireOp",EDGE,"E4"),sQuery(id+"F0.wireOp",EDGE,"E5"),sQuery(id+"F0.wireOp",EDGE,"E6"),sQuery(id+"F0.wireOp",EDGE,"E7"),subQ1,subQ0,sQuery(id+"F0.wireOp",EDGE,"E10"),sQuery(id+"F0.wireOp",EDGE,"E11"),sQuery(id+"F0.wireOp",EDGE,"E12"),sQuery(id+"F0.wireOp",EDGE,"E13"),sQuery(id+"F0.wireOp",EDGE,"E14"),sQuery(id+"F0.wireOp",EDGE,"E15")])],"isStart":true})],"blendedInto":[makeQuery(id+"F1.opExtrude","CAP_FACE",FACE,{"disambiguationData":[OSD([sQuery(id+"F0.wireOp",EDGE,"E0"),sQuery(id+"F0.wireOp",EDGE,"E1"),sQuery(id+"F0.wireOp",EDGE,"E2"),sQuery(id+"F0.wireOp",EDGE,"E3"),sQuery(id+"F0.wireOp",EDGE,"E4"),sQuery(id+"F0.wireOp",EDGE,"E5"),sQuery(id+"F0.wireOp",EDGE,"E6"),sQuery(id+"F0.wireOp",EDGE,"E7"),subQ1,subQ0,sQuery(id+"F0.wireOp",EDGE,"E10"),sQuery(id+"F0.wireOp",EDGE,"E11"),sQuery(id+"F0.wireOp",EDGE,"E12"),sQuery(id+"F0.wireOp",EDGE,"E13"),sQuery(id+"F0.wireOp",EDGE,"E14"),sQuery(id+"F0.wireOp",EDGE,"E15")])],"isStart":true})]});}
            var Q19;
            Q19=makeQuery(id+"F1.opExtrude","CAP_EDGE",EDGE,{"disambiguationData":[OSD([sQuery(id+"F0.wireOp",EDGE,"E9")])],"isStart":true});
            var Q20;
            {var subQ0=sQuery(id+"F0.wireOp",EDGE,"E10");var subQ1=sQuery(id+"F0.wireOp",EDGE,"E9");Q20=makeQuery(id+"F3.opFillet","BLEND_EDGE",EDGE,{"blendedFrom":[makeQuery(id+"F1.opExtrude","SWEPT_EDGE",EDGE,{"disambiguationData":[OSD([subQ1,subQ0])]}),makeQuery(id+"F1.opExtrude","CAP_FACE",FACE,{"disambiguationData":[OSD([sQuery(id+"F0.wireOp",EDGE,"E0"),sQuery(id+"F0.wireOp",EDGE,"E1"),sQuery(id+"F0.wireOp",EDGE,"E2"),sQuery(id+"F0.wireOp",EDGE,"E3"),sQuery(id+"F0.wireOp",EDGE,"E4"),sQuery(id+"F0.wireOp",EDGE,"E5"),sQuery(id+"F0.wireOp",EDGE,"E6"),sQuery(id+"F0.wireOp",EDGE,"E7"),sQuery(id+"F0.wireOp",EDGE,"E8"),subQ1,subQ0,sQuery(id+"F0.wireOp",EDGE,"E11"),sQuery(id+"F0.wireOp",EDGE,"E12"),sQuery(id+"F0.wireOp",EDGE,"E13"),sQuery(id+"F0.wireOp",EDGE,"E14"),sQuery(id+"F0.wireOp",EDGE,"E15")])],"isStart":true})],"blendedInto":[makeQuery(id+"F1.opExtrude","CAP_FACE",FACE,{"disambiguationData":[OSD([sQuery(id+"F0.wireOp",EDGE,"E0"),sQuery(id+"F0.wireOp",EDGE,"E1"),sQuery(id+"F0.wireOp",EDGE,"E2"),sQuery(id+"F0.wireOp",EDGE,"E3"),sQuery(id+"F0.wireOp",EDGE,"E4"),sQuery(id+"F0.wireOp",EDGE,"E5"),sQuery(id+"F0.wireOp",EDGE,"E6"),sQuery(id+"F0.wireOp",EDGE,"E7"),sQuery(id+"F0.wireOp",EDGE,"E8"),subQ1,subQ0,sQuery(id+"F0.wireOp",EDGE,"E11"),sQuery(id+"F0.wireOp",EDGE,"E12"),sQuery(id+"F0.wireOp",EDGE,"E13"),sQuery(id+"F0.wireOp",EDGE,"E14"),sQuery(id+"F0.wireOp",EDGE,"E15")])],"isStart":true})]});}
            var Q21;
            Q21=makeQuery(id+"F1.opExtrude","CAP_EDGE",EDGE,{"disambiguationData":[OSD([sQuery(id+"F0.wireOp",EDGE,"E10")])],"isStart":true});
            fillet(context, id + "F9", {"entities" : qUnion([Q0, Q1, Q2, Q3, Q4, Q5, Q6, Q7, Q8, Q9, Q10, Q11, Q12, Q13, Q14, Q15, Q16, Q17, Q18, Q19, Q20, Q21]), "radius" : 0.4 * mm, "tangentPropagation" : true, "allowEdgeOverflow" : false});
        }
        {
            var Q0;
            Q0=makeQuery(id+"F1.opExtrude","CAP_EDGE",EDGE,{"disambiguationData":[OSD([sQuery(id+"F0.wireOp",EDGE,"E13")])],"isStart":true});
            chamfer(context, id + "F10", {"entities" : qUnion([Q0]), "width" : 0.4 * mm, "tangentPropagation" : true});
        }
        {
            var Q0;
            Q0=makeQuery(id+"F1.opExtrude","CAP_EDGE",EDGE,{"disambiguationData":[OSD([sQuery(id+"F0.wireOp",EDGE,"E13")])],"isStart":false});
            chamfer(context, id + "F11", {"entities" : qUnion([Q0]), "width" : 0.4 * mm, "tangentPropagation" : true});
        }
    });
